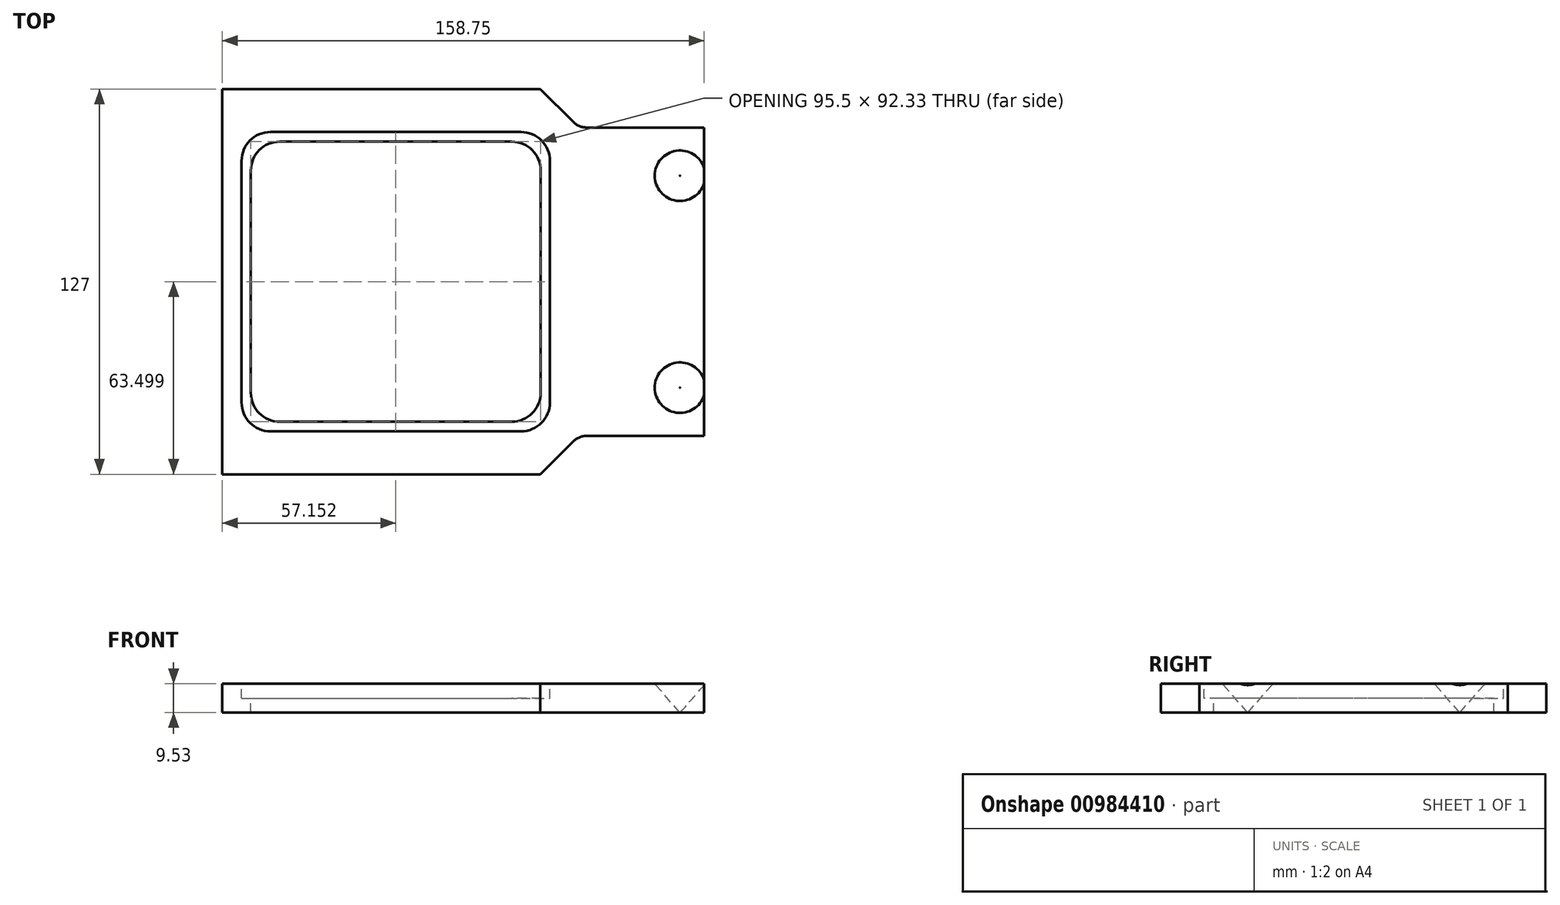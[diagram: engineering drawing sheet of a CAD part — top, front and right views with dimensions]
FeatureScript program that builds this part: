
annotation { "Feature Type Name" : "Feature", "Feature Type Description" : "" }
export const myFeature = defineFeature(function(context is Context, id is Id, definition is map)
    precondition{}
    {
        {
            var Q0;
            Q0=qCreatedBy(makeId("Top.planeOp"),FACE);
            var sketch = newSketch(context, id + "F0", { "sketchPlane" : qUnion([Q0])});
            skLineSegment(sketch, "E0.bottom", {"start": v(-66.88, 57.45) * mm, "end": v(37.9, 57.45) * mm});
            skLineSegment(sketch, "E0.top", {"start": v(-66.88, -69.55) * mm, "end": v(37.9, -69.55) * mm});
            skLineSegment(sketch, "E0.left", {"start": v(-66.88, 57.45) * mm, "end": v(-66.88, -69.55) * mm});
            skLineSegment(sketch, "E0.right", {"start": v(91.87, 44.75) * mm, "end": v(91.87, -56.85) * mm});
            skLineSegment(sketch, "E1", {"start": v(37.9, 57.45) * mm, "end": v(48.74, 46.6) * mm});
            skLineSegment(sketch, "E2", {"start": v(53.23, 44.75) * mm, "end": v(91.87, 44.75) * mm});
            skLineSegment(sketch, "E3", {"start": v(37.9, -69.55) * mm, "end": v(48.74, -58.71) * mm});
            skLineSegment(sketch, "E4", {"start": v(53.23, -56.85) * mm, "end": v(91.87, -56.85) * mm});
            skArc(sketch, "E5.filletArc", {"start": v(53.23, -56.85) * mm, "mid": v(50.8, -57.33) * mm, "end": v(48.74, -58.71) * mm});
            skArc(sketch, "E6.filletArc", {"start": v(48.74, 46.6) * mm, "mid": v(50.8, 45.23) * mm, "end": v(53.23, 44.75) * mm});
            skSolve(sketch);
        }
        {
            var Q0;
            Q0=makeQuery(id+"F0.imprint","IMPRINT",FACE,{"disambiguationData":[TD([[makeQuery(id+"F0.imprint","IMPRINT",EDGE,{"derivedFrom":sQuery(id+"F0.wireOp",EDGE,"E0.bottom")}),-1.0]])]});
            extrude(context, id + "F1", {"entities" : qUnion([Q0]), "depth" : 9.52 * mm, "offsetDistance" : 25.4 * mm});
        }
        {
            var Q0;
            Q0=makeQuery(id+"F1.opExtrude","CAP_FACE",FACE,{"disambiguationData":[OSD([sQuery(id+"F0.wireOp",EDGE,"E0.bottom"),sQuery(id+"F0.wireOp",EDGE,"E0.top"),sQuery(id+"F0.wireOp",EDGE,"E0.left"),sQuery(id+"F0.wireOp",EDGE,"E0.right"),sQuery(id+"F0.wireOp",EDGE,"E1"),sQuery(id+"F0.wireOp",EDGE,"E2"),sQuery(id+"F0.wireOp",EDGE,"E3"),sQuery(id+"F0.wireOp",EDGE,"E4"),sQuery(id+"F0.wireOp",EDGE,"E5.filletArc"),sQuery(id+"F0.wireOp",EDGE,"E6.filletArc")])],"isStart":false});
            var sketch = newSketch(context, id + "F2", { "sketchPlane" : qUnion([Q0])});
            skLineSegment(sketch, "E7", {"start": v(-66.88, -6.05) * mm, "end": v(91.87, -6.05) * mm, "construction": true});
            skPoint(sketch, "E8", {"position": v(-9.73, -6.05) * mm});
            skLineSegment(sketch, "E9.bottom", {"start": v(-47.96, 40.11) * mm, "end": v(28.5, 40.11) * mm});
            skLineSegment(sketch, "E9.top", {"start": v(-47.96, -52.22) * mm, "end": v(28.5, -52.22) * mm});
            skLineSegment(sketch, "E9.left", {"start": v(-57.48, 30.59) * mm, "end": v(-57.48, -42.7) * mm});
            skLineSegment(sketch, "E9.right", {"start": v(38.02, 30.59) * mm, "end": v(38.02, -42.7) * mm});
            skLineSegment(sketch, "E10.bottom", {"start": v(-51, 43.29) * mm, "end": v(31.55, 43.29) * mm});
            skLineSegment(sketch, "E10.top", {"start": v(-51, -55.4) * mm, "end": v(31.55, -55.4) * mm});
            skLineSegment(sketch, "E10.left", {"start": v(-60.53, 33.76) * mm, "end": v(-60.53, -45.87) * mm});
            skLineSegment(sketch, "E10.right", {"start": v(41.07, 33.76) * mm, "end": v(41.07, -45.87) * mm});
            skPoint(sketch, "E11.visualSharp", {"position": v(-57.48, 40.11) * mm});
            skArc(sketch, "E11.filletArc", {"start": v(-47.96, 40.11) * mm, "mid": v(-54.7, 37.32) * mm, "end": v(-57.48, 30.59) * mm});
            skPoint(sketch, "E12.visualSharp", {"position": v(-57.48, -52.22) * mm});
            skArc(sketch, "E12.filletArc", {"start": v(-57.48, -42.7) * mm, "mid": v(-54.7, -49.43) * mm, "end": v(-47.96, -52.22) * mm});
            skPoint(sketch, "E13.visualSharp", {"position": v(38.02, -52.22) * mm});
            skArc(sketch, "E13.filletArc", {"start": v(28.5, -52.22) * mm, "mid": v(35.23, -49.43) * mm, "end": v(38.02, -42.7) * mm});
            skPoint(sketch, "E14.visualSharp", {"position": v(38.02, 40.11) * mm});
            skArc(sketch, "E14.filletArc", {"start": v(38.02, 30.59) * mm, "mid": v(35.23, 37.32) * mm, "end": v(28.5, 40.11) * mm});
            skPoint(sketch, "E15.visualSharp", {"position": v(-60.53, 43.29) * mm});
            skArc(sketch, "E15.filletArc", {"start": v(-51, 43.29) * mm, "mid": v(-57.74, 40.5) * mm, "end": v(-60.53, 33.76) * mm});
            skPoint(sketch, "E16.visualSharp", {"position": v(-60.53, -55.4) * mm});
            skArc(sketch, "E16.filletArc", {"start": v(-60.53, -45.87) * mm, "mid": v(-57.74, -52.6) * mm, "end": v(-51, -55.4) * mm});
            skPoint(sketch, "E17.visualSharp", {"position": v(41.07, -55.4) * mm});
            skArc(sketch, "E17.filletArc", {"start": v(31.55, -55.4) * mm, "mid": v(38.28, -52.6) * mm, "end": v(41.07, -45.87) * mm});
            skPoint(sketch, "E18.visualSharp", {"position": v(41.07, 43.29) * mm});
            skArc(sketch, "E18.filletArc", {"start": v(41.07, 33.76) * mm, "mid": v(38.28, 40.5) * mm, "end": v(31.55, 43.29) * mm});
            skPoint(sketch, "E19", {"position": v(83.92, 28.87) * mm});
            skPoint(sketch, "E20", {"position": v(83.92, -40.98) * mm});
            skSolve(sketch);
        }
        {
            var Q0;
            Q0=makeQuery(id+"F2.imprint","IMPRINT",FACE,{"disambiguationData":[TD([[makeQuery(id+"F2.imprint","IMPRINT",EDGE,{"derivedFrom":sQuery(id+"F2.wireOp",EDGE,"E9.bottom")}),1.0]])]});
            extrude(context, id + "F3", {"entities" : qUnion([Q0]), "operationType" : NewBodyOperationType.REMOVE, "oppositeDirection" : true, "depth" : 4.78 * mm, "offsetDistance" : 25.4 * mm});
        }
        {
            var Q0;
            Q0=makeQuery(id+"F3.boolean.opBoolean","SPLIT",FACE,{"disambiguationData":[TD([makeQuery(id+"F3.opExtrude","SWEPT_FACE",FACE,{"disambiguationData":[OSD([sQuery(id+"F2.wireOp",EDGE,"E9.bottom")])]})])],"derivedFrom":makeQuery(id+"F1.opExtrude","CAP_FACE",FACE,{"disambiguationData":[OSD([sQuery(id+"F0.wireOp",EDGE,"E0.bottom"),sQuery(id+"F0.wireOp",EDGE,"E0.top"),sQuery(id+"F0.wireOp",EDGE,"E0.left"),sQuery(id+"F0.wireOp",EDGE,"E0.right"),sQuery(id+"F0.wireOp",EDGE,"E1"),sQuery(id+"F0.wireOp",EDGE,"E2"),sQuery(id+"F0.wireOp",EDGE,"E3"),sQuery(id+"F0.wireOp",EDGE,"E4"),sQuery(id+"F0.wireOp",EDGE,"E5.filletArc"),sQuery(id+"F0.wireOp",EDGE,"E6.filletArc")])],"isStart":false})});
            extrude(context, id + "F4", {"entities" : qUnion([Q0]), "operationType" : NewBodyOperationType.REMOVE, "endBound" : BoundingType.THROUGH_ALL, "oppositeDirection" : true, "depth" : 25.4 * mm, "offsetDistance" : 25.4 * mm});
        }
        {
            var Q0;
            {var subQ0=sQuery(id+"F0.wireOp",EDGE,"E5.filletArc");var subQ1=sQuery(id+"F0.wireOp",EDGE,"E4");var subQ2=sQuery(id+"F0.wireOp",EDGE,"E3");var subQ3=sQuery(id+"F0.wireOp",EDGE,"E2");var subQ4=sQuery(id+"F0.wireOp",EDGE,"E1");var subQ5=sQuery(id+"F0.wireOp",EDGE,"E6.filletArc");var subQ6=sQuery(id+"F0.wireOp",EDGE,"E0.bottom");var subQ7=sQuery(id+"F0.wireOp",EDGE,"E0.right");var subQ8=sQuery(id+"F0.wireOp",EDGE,"E0.top");var subQ9=sQuery(id+"F0.wireOp",EDGE,"E0.left");Q0=makeQuery(id+"F3.boolean.opBoolean","SPLIT",FACE,{"disambiguationData":[TD([makeQuery(id+"F1.opExtrude","SWEPT_FACE",FACE,{"disambiguationData":[OSD([subQ6])]})])],"derivedFrom":makeQuery(id+"F1.opExtrude","CAP_FACE",FACE,{"disambiguationData":[OSD([subQ6,subQ8,subQ9,subQ7,subQ4,subQ3,subQ2,subQ1,subQ0,subQ5])],"isStart":false})});}
            var sketch = newSketch(context, id + "F5", { "sketchPlane" : qUnion([Q0])});
            skPoint(sketch, "E21", {"position": v(83.92, 28.87) * mm});
            skPoint(sketch, "E22", {"position": v(83.92, -40.98) * mm});
            skSolve(sketch);
        }
        {
            var Q0;
            Q0=sQuery(id+"F5.wireOp",VERTEX,"E21");
            var Q1;
            Q1=sQuery(id+"F5.wireOp",VERTEX,"E22");
            var Q2;
            Q2=makeQuery(id+"F1.opExtrude","SWEPT_BODY",BODY,{"disambiguationData":[OSD([sQuery(id+"F0.wireOp",EDGE,"E0.bottom"),sQuery(id+"F0.wireOp",EDGE,"E0.top"),sQuery(id+"F0.wireOp",EDGE,"E0.left"),sQuery(id+"F0.wireOp",EDGE,"E0.right"),sQuery(id+"F0.wireOp",EDGE,"E1"),sQuery(id+"F0.wireOp",EDGE,"E2"),sQuery(id+"F0.wireOp",EDGE,"E3"),sQuery(id+"F0.wireOp",EDGE,"E4"),sQuery(id+"F0.wireOp",EDGE,"E5.filletArc"),sQuery(id+"F0.wireOp",EDGE,"E6.filletArc")])]});
            hole(context, id + "F6", {"style" : HoleStyle.C_SINK, "endStyle" : HoleEndStyle.THROUGH, "standardTappedOrClearance" : lookupTablePath({ "standard" : "ANSI", "size" : "11/32 (0.34)", "type" : "Drilled" }), "standardBlindInLast" : lookupTablePath({ "standard" : "ANSI", "size" : "11/32 (0.34)", "type" : "Drilled" }), "holeDiameter" : 11 / 812.8 * mm, "cSinkDiameter" : 16.66 * mm, "cSinkAngle" : 82 * degree, "majorDiameter" : 12.7 * mm, "isTappedThrough" : true, "tappedDepth" : 92.56 * mm, "tapClearance" : 3, "locations" : qUnion([Q0, Q1]), "scope" : qUnion([Q2])});
        }
    });
